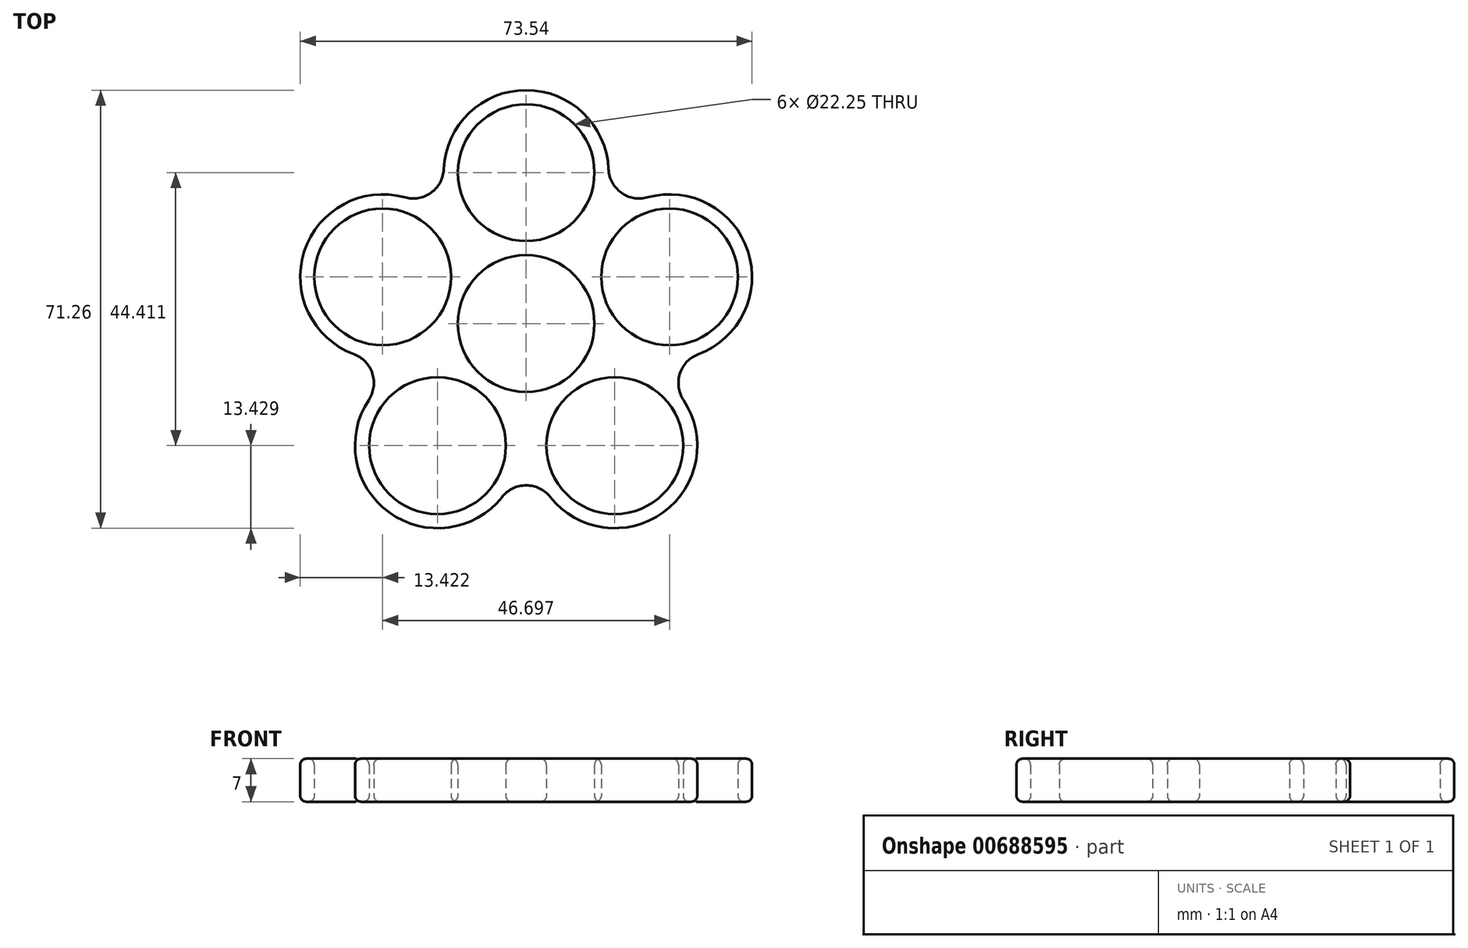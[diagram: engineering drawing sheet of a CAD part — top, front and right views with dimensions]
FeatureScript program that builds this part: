
annotation { "Feature Type Name" : "Feature", "Feature Type Description" : "" }
export const myFeature = defineFeature(function(context is Context, id is Id, definition is map)
    precondition{}
    {
        {
            var Q0;
            Q0=qCreatedBy(makeId("Top.planeOp"),FACE);
            var sketch = newSketch(context, id + "F0", { "sketchPlane" : qUnion([Q0])});
            skCircle(sketch, "E0", {"center": v(0, 0) * mm, "radius": 11.12 * mm});
            skLineSegment(sketch, "E1", {"start": v(0, 0) * mm, "end": v(0, 24.55) * mm, "construction": true});
            skLineSegment(sketch, "E2", {"start": v(0, 0) * mm, "end": v(23.35, 7.59) * mm, "construction": true});
            skLineSegment(sketch, "E3", {"start": v(0, 0) * mm, "end": v(14.43, -19.86) * mm, "construction": true});
            skLineSegment(sketch, "E4", {"start": v(0, 0) * mm, "end": v(-23.35, 7.59) * mm, "construction": true});
            skLineSegment(sketch, "E5", {"start": v(0, 0) * mm, "end": v(-14.43, -19.86) * mm, "construction": true});
            skCircle(sketch, "E6", {"center": v(0, 24.55) * mm, "radius": 11.12 * mm});
            skCircle(sketch, "E7", {"center": v(-23.35, 7.59) * mm, "radius": 11.12 * mm});
            skCircle(sketch, "E8", {"center": v(-14.43, -19.86) * mm, "radius": 11.12 * mm});
            skCircle(sketch, "E9", {"center": v(14.43, -19.86) * mm, "radius": 11.12 * mm});
            skCircle(sketch, "E10", {"center": v(23.35, 7.59) * mm, "radius": 11.12 * mm});
            skArc(sketch, "E11", {"start": v(13.41, 25.12) * mm, "mid": v(0, 37.97) * mm, "end": v(-13.41, 25.12) * mm});
            skArc(sketch, "E12", {"start": v(-19.75, 20.52) * mm, "mid": v(-36.12, 11.73) * mm, "end": v(-28.04, -5) * mm});
            skArc(sketch, "E13", {"start": v(-25.62, -12.44) * mm, "mid": v(-22.32, -30.72) * mm, "end": v(-3.92, -28.2) * mm});
            skArc(sketch, "E14", {"start": v(3.92, -28.2) * mm, "mid": v(22.32, -30.72) * mm, "end": v(25.62, -12.44) * mm});
            skArc(sketch, "E15", {"start": v(28.04, -5) * mm, "mid": v(36.12, 11.73) * mm, "end": v(19.75, 20.52) * mm});
            skArc(sketch, "E16", {"start": v(-19.75, 20.52) * mm, "mid": v(-15.47, 21.3) * mm, "end": v(-13.41, 25.12) * mm});
            skArc(sketch, "E17", {"start": v(-25.62, -12.44) * mm, "mid": v(-25.03, -8.13) * mm, "end": v(-28.04, -5) * mm});
            skArc(sketch, "E18", {"start": v(3.92, -28.2) * mm, "mid": v(0, -26.32) * mm, "end": v(-3.92, -28.2) * mm});
            skArc(sketch, "E19", {"start": v(13.41, 25.12) * mm, "mid": v(15.47, 21.3) * mm, "end": v(19.75, 20.52) * mm});
            skArc(sketch, "E20", {"start": v(28.04, -5) * mm, "mid": v(25.03, -8.13) * mm, "end": v(25.62, -12.44) * mm});
            skSolve(sketch);
        }
        {
            var Q0;
            Q0=makeQuery(id+"F0.imprint","IMPRINT",FACE,{"disambiguationData":[TD([[makeQuery(id+"F0.imprint","IMPRINT",EDGE,{"derivedFrom":sQuery(id+"F0.wireOp",EDGE,"E0")}),-1.0]])]});
            extrude(context, id + "F1", {"entities" : qUnion([Q0]), "depth" : 7 * mm, "offsetDistance" : 25 * mm});
        }
        {
            var Q0;
            Q0=makeQuery(id+"F1.opExtrude","CAP_EDGE",EDGE,{"disambiguationData":[OSD([sQuery(id+"F0.wireOp",EDGE,"E12")])],"isStart":false});
            var Q1;
            Q1=makeQuery(id+"F1.opExtrude","CAP_EDGE",EDGE,{"disambiguationData":[OSD([sQuery(id+"F0.wireOp",EDGE,"E13")])],"isStart":true});
            var Q2;
            Q2=makeQuery(id+"F1.opExtrude","CAP_EDGE",EDGE,{"disambiguationData":[OSD([sQuery(id+"F0.wireOp",EDGE,"E8")])],"isStart":false});
            var Q3;
            Q3=makeQuery(id+"F1.opExtrude","CAP_EDGE",EDGE,{"disambiguationData":[OSD([sQuery(id+"F0.wireOp",EDGE,"E7")])],"isStart":false});
            var Q4;
            Q4=makeQuery(id+"F1.opExtrude","CAP_EDGE",EDGE,{"disambiguationData":[OSD([sQuery(id+"F0.wireOp",EDGE,"E6")])],"isStart":true});
            var Q5;
            Q5=makeQuery(id+"F1.opExtrude","CAP_EDGE",EDGE,{"disambiguationData":[OSD([sQuery(id+"F0.wireOp",EDGE,"E6")])],"isStart":false});
            var Q6;
            Q6=makeQuery(id+"F1.opExtrude","CAP_EDGE",EDGE,{"disambiguationData":[OSD([sQuery(id+"F0.wireOp",EDGE,"E7")])],"isStart":true});
            var Q7;
            Q7=makeQuery(id+"F1.opExtrude","CAP_EDGE",EDGE,{"disambiguationData":[OSD([sQuery(id+"F0.wireOp",EDGE,"E8")])],"isStart":true});
            var Q8;
            Q8=makeQuery(id+"F1.opExtrude","CAP_EDGE",EDGE,{"disambiguationData":[OSD([sQuery(id+"F0.wireOp",EDGE,"E0")])],"isStart":true});
            var Q9;
            Q9=makeQuery(id+"F1.opExtrude","CAP_EDGE",EDGE,{"disambiguationData":[OSD([sQuery(id+"F0.wireOp",EDGE,"E0")])],"isStart":false});
            var Q10;
            Q10=makeQuery(id+"F1.opExtrude","CAP_EDGE",EDGE,{"disambiguationData":[OSD([sQuery(id+"F0.wireOp",EDGE,"E10")])],"isStart":true});
            var Q11;
            Q11=makeQuery(id+"F1.opExtrude","CAP_EDGE",EDGE,{"disambiguationData":[OSD([sQuery(id+"F0.wireOp",EDGE,"E10")])],"isStart":false});
            var Q12;
            Q12=makeQuery(id+"F1.opExtrude","CAP_EDGE",EDGE,{"disambiguationData":[OSD([sQuery(id+"F0.wireOp",EDGE,"E9")])],"isStart":true});
            var Q13;
            Q13=makeQuery(id+"F1.opExtrude","CAP_EDGE",EDGE,{"disambiguationData":[OSD([sQuery(id+"F0.wireOp",EDGE,"E9")])],"isStart":false});
            fillet(context, id + "F2", {"entities" : qUnion([Q0, Q1, Q2, Q3, Q4, Q5, Q6, Q7, Q8, Q9, Q10, Q11, Q12, Q13]), "radius" : 1 * mm, "tangentPropagation" : true, "allowEdgeOverflow" : false});
        }
    });
